# Revit family: KEUCO_14971010000__
name_source: partatom
category: Generic Models
revit_build: Autodesk Revit 2016 (Build: 20150220_1215(x64)
units: mm (PartAtom-declared; Revit-internal decimal feet)

## family parameters
Always vertical = No
Can host rebar = No
Cut with Voids When Loaded = No
Part Type = Normal
Room Calculation Point = No
Round Connector Dimension = Use Diameter
Shared = No
Work Plane-Based = Yes

## types (3) — shared parameters
Default Elevation = 1219 mm
Description = Symbol Damen / Herren
Gewicht = 2.718
Kategorie = ACC
Manufacturer = KEUCO
Rail Length = 851 mm  [stored 2.79199 ft]
Serie = Plan
URL = https://www.keuco.com
Verwendung = ZU

## per-type parameters (varying)
| type | Ausschreibungstext | Material |
| 14971010000 | KEUCO PLAN Türschild 14971010000 Damen / Herren
Hochglanzverchromtes Türschild 
mit dem Symbol DAMEN/HERREN 
in quadratischer Form, 
mit abgerundeten Ecken, 
Maße 100 x 100 mm | Verchromt |
| 14971070000 | KEUCO PLAN Türschild 14971070000 Damen / Herren
Türschild aus hochwertigem Edelstahl 
mit dem Symbol DAMEN/HERREN 
in quadratischer Form, 
mit abgerundeten Ecken, 
Maße 100 x 100 mm | Edelstahl |
| 14971170000 | KEUCO PLAN Türschild 14971170000 Damen / Herren
Türschild aus silber-eloxiertem Aluminium (E6 EV1) 
mit dem Symbol DAEMN/HERREN 
in quadratischer Form, 
mit abgerundeten Ecken, 
Maße 100 x 100 mm | Verchromt |

note: column(s) folded — value = type name in every type: Artikelnummer

note: [stored X ft] marks values corroborated as IEEE doubles in the binary element streams (Revit-internal decimal feet)

## geometry (parser evidence)
native form markers: Sweep x3
no freeform markers — native parametric forms only
